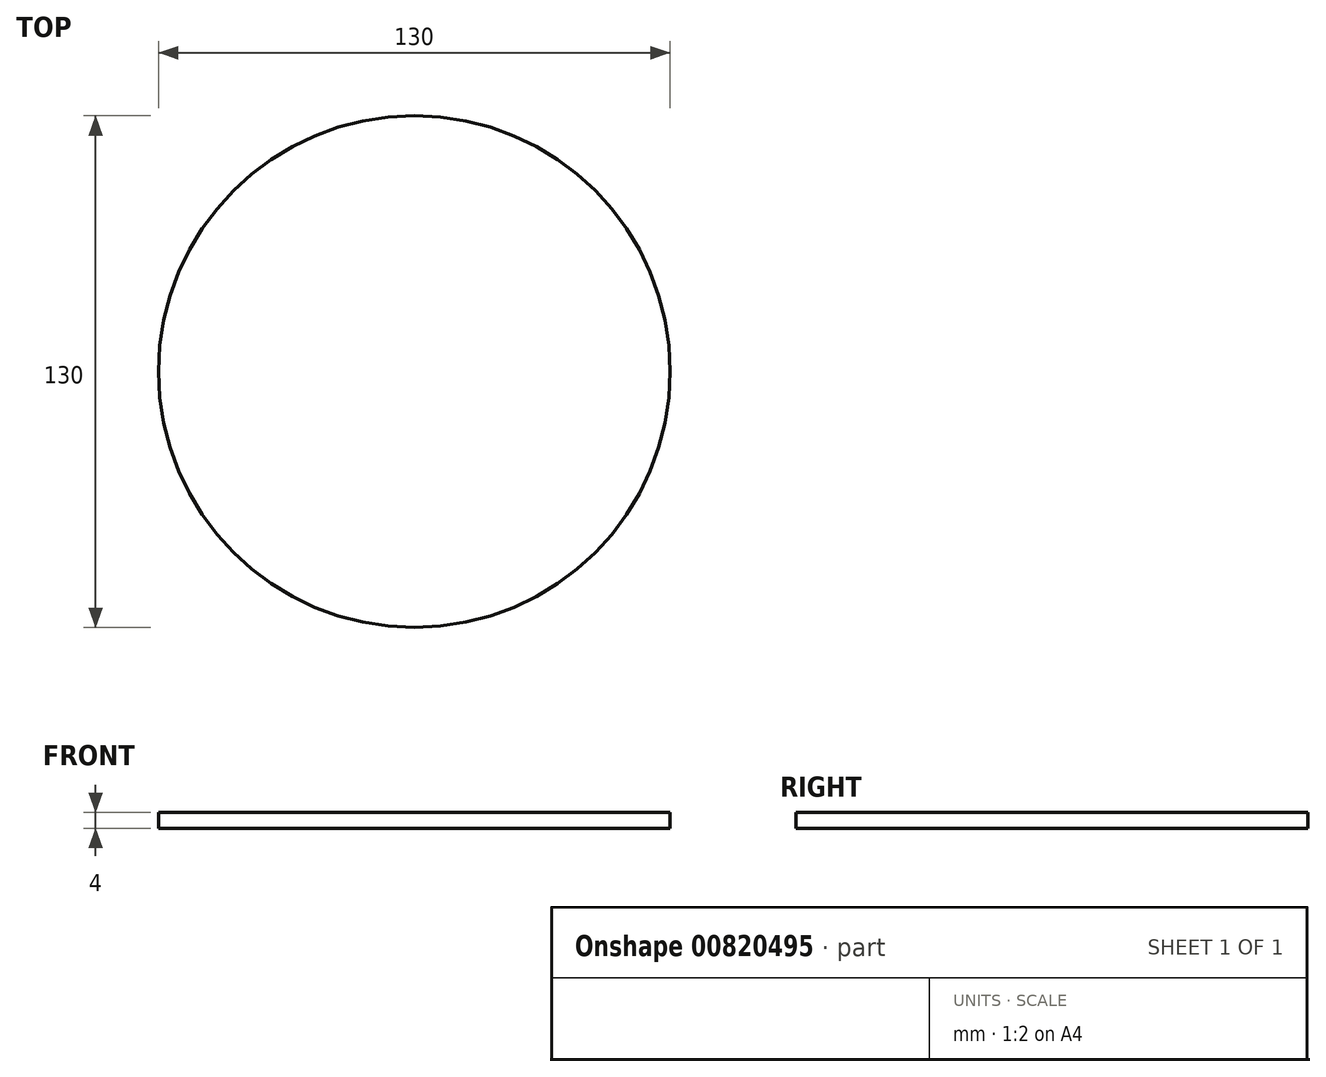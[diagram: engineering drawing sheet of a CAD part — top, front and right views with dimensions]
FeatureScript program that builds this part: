
annotation { "Feature Type Name" : "Feature", "Feature Type Description" : "" }
export const myFeature = defineFeature(function(context is Context, id is Id, definition is map)
    precondition{}
    {
        {
            var Q0;
            Q0=qCreatedBy(makeId("Top.planeOp"),FACE);
            var sketch = newSketch(context, id + "F0", { "sketchPlane" : qUnion([Q0])});
            skCircle(sketch, "E0", {"center": v(0, 0) * mm, "radius": 65 * mm});
            skSolve(sketch);
        }
        {
            var Q0;
            Q0=makeQuery(id+"F0.imprint","IMPRINT",FACE,{"disambiguationData":[TD([[makeQuery(id+"F0.imprint","IMPRINT",EDGE,{"derivedFrom":sQuery(id+"F0.wireOp",EDGE,"E0")}),1.0]])]});
            extrude(context, id + "F1", {"entities" : qUnion([Q0]), "depth" : 4 * mm, "offsetDistance" : 25 * mm});
        }
    });
